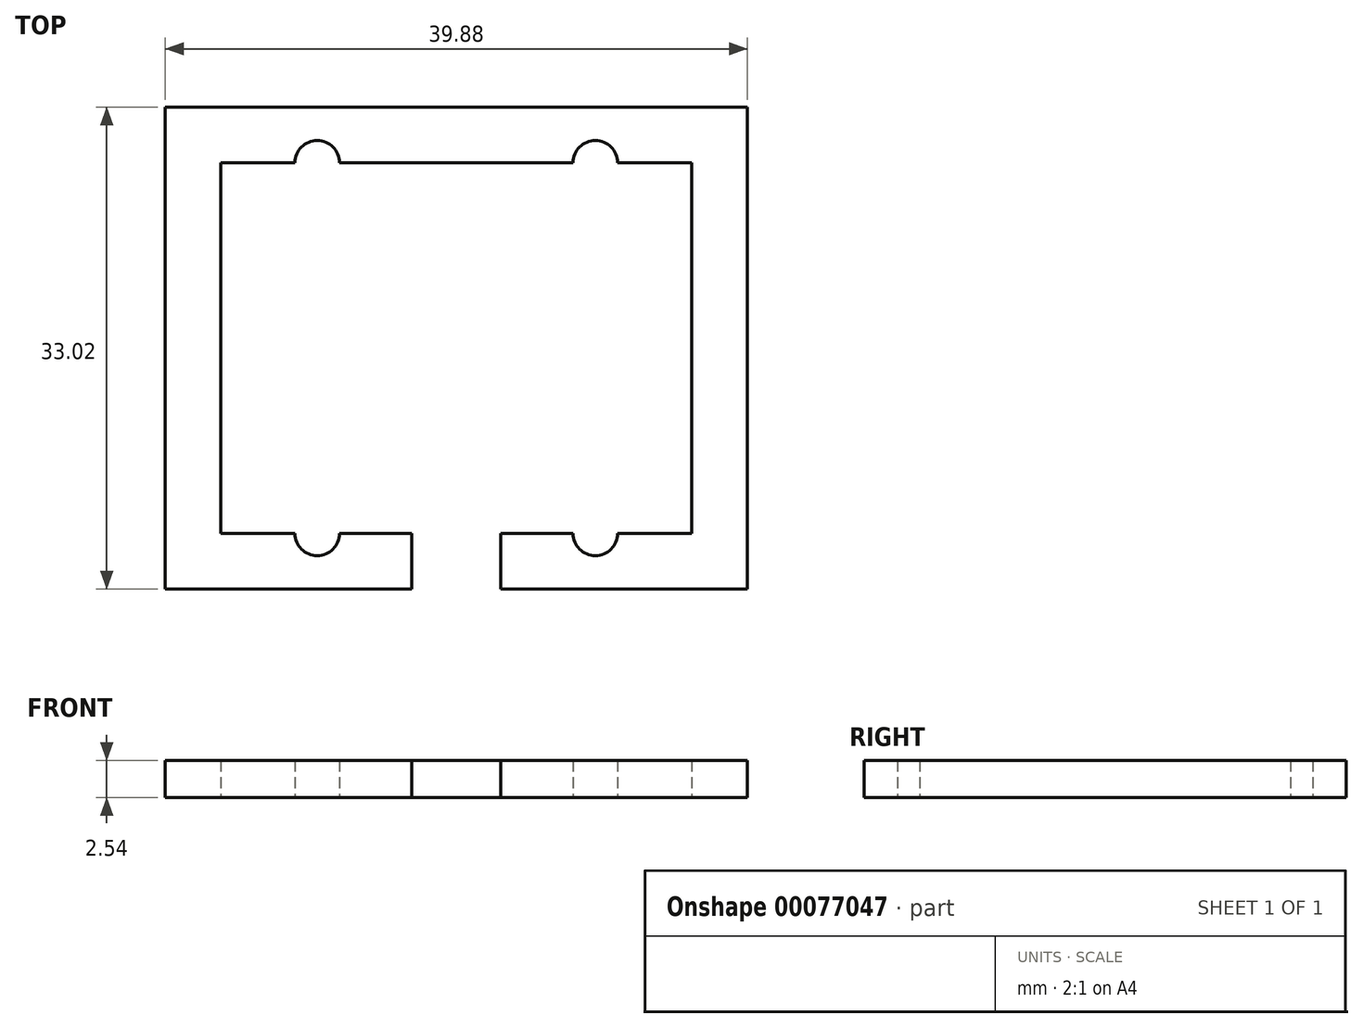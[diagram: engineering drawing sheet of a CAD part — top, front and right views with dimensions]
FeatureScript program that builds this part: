
annotation { "Feature Type Name" : "Feature", "Feature Type Description" : "" }
export const myFeature = defineFeature(function(context is Context, id is Id, definition is map)
    precondition{}
    {
        {
            var Q0;
            Q0=qCreatedBy(makeId("Top.planeOp"),FACE);
            var sketch = newSketch(context, id + "F0", { "sketchPlane" : qUnion([Q0])});
            skLineSegment(sketch, "E0.bottom", {"start": v(-19.94, 16.51) * mm, "end": v(19.94, 16.51) * mm});
            skLineSegment(sketch, "E0.top", {"start": v(-19.94, -16.51) * mm, "end": v(19.94, -16.51) * mm});
            skLineSegment(sketch, "E0.left", {"start": v(-19.94, 16.51) * mm, "end": v(-19.94, -16.51) * mm});
            skLineSegment(sketch, "E0.right", {"start": v(19.94, 16.51) * mm, "end": v(19.94, -16.51) * mm});
            skPoint(sketch, "E0.middle", {"position": v(0, 0) * mm});
            skLineSegment(sketch, "E1.left", {"start": v(16.13, 12.7) * mm, "end": v(16.13, -12.7) * mm});
            skLineSegment(sketch, "E1.right", {"start": v(-16.13, 12.7) * mm, "end": v(-16.13, -12.7) * mm});
            skPoint(sketch, "E2.middle", {"position": v(0, 16.51) * mm});
            skLineSegment(sketch, "E3", {"start": v(-35.4, 0) * mm, "end": v(32.75, 0) * mm, "construction": true});
            skLineSegment(sketch, "E4", {"start": v(0, 34) * mm, "end": v(0, -24.9) * mm, "construction": true});
            skPoint(sketch, "E5.middle", {"position": v(-19.94, 0) * mm});
            skCircle(sketch, "E6", {"center": v(-9.52, 12.7) * mm, "radius": 1.52 * mm});
            skCircle(sketch, "E7.MirrorC", {"center": v(9.52, 12.7) * mm, "radius": 1.52 * mm});
            skCircle(sketch, "E8.MirrorC", {"center": v(-9.53, -12.7) * mm, "radius": 1.52 * mm});
            skCircle(sketch, "E9.MirrorC", {"center": v(9.52, -12.7) * mm, "radius": 1.52 * mm});
            skLineSegment(sketch, "E10", {"start": v(-16.13, 12.7) * mm, "end": v(-11.05, 12.7) * mm});
            skLineSegment(sketch, "E11", {"start": v(-8, 12.7) * mm, "end": v(8, 12.7) * mm});
            skLineSegment(sketch, "E12", {"start": v(11.05, 12.7) * mm, "end": v(16.13, 12.7) * mm});
            skLineSegment(sketch, "E13", {"start": v(16.13, -12.7) * mm, "end": v(11.05, -12.7) * mm});
            skLineSegment(sketch, "E14", {"start": v(-11.05, -12.7) * mm, "end": v(-16.13, -12.7) * mm});
            skPoint(sketch, "E15.middle", {"position": v(0, -14.76) * mm});
            skLineSegment(sketch, "E16", {"start": v(-3.05, -12.7) * mm, "end": v(-3.05, -16.51) * mm});
            skLineSegment(sketch, "E17", {"start": v(-3.05, -16.51) * mm, "end": v(3.05, -16.51) * mm});
            skLineSegment(sketch, "E18", {"start": v(3.05, -16.51) * mm, "end": v(3.05, -12.7) * mm});
            skLineSegment(sketch, "E19", {"start": v(-3.05, -12.7) * mm, "end": v(-8, -12.7) * mm});
            skLineSegment(sketch, "E20", {"start": v(3.05, -12.7) * mm, "end": v(8, -12.7) * mm});
            skSolve(sketch);
        }
        {
            var Q0;
            Q0=makeQuery(id+"F0.imprint","IMPRINT",FACE,{"disambiguationData":[TD([[makeQuery(id+"F0.imprint","IMPRINT",EDGE,{"derivedFrom":sQuery(id+"F0.wireOp",EDGE,"E0.bottom")}),-1.0]])]});
            extrude(context, id + "F1", {"entities" : qUnion([Q0]), "depth" : 2.54 * mm});
        }
    });
